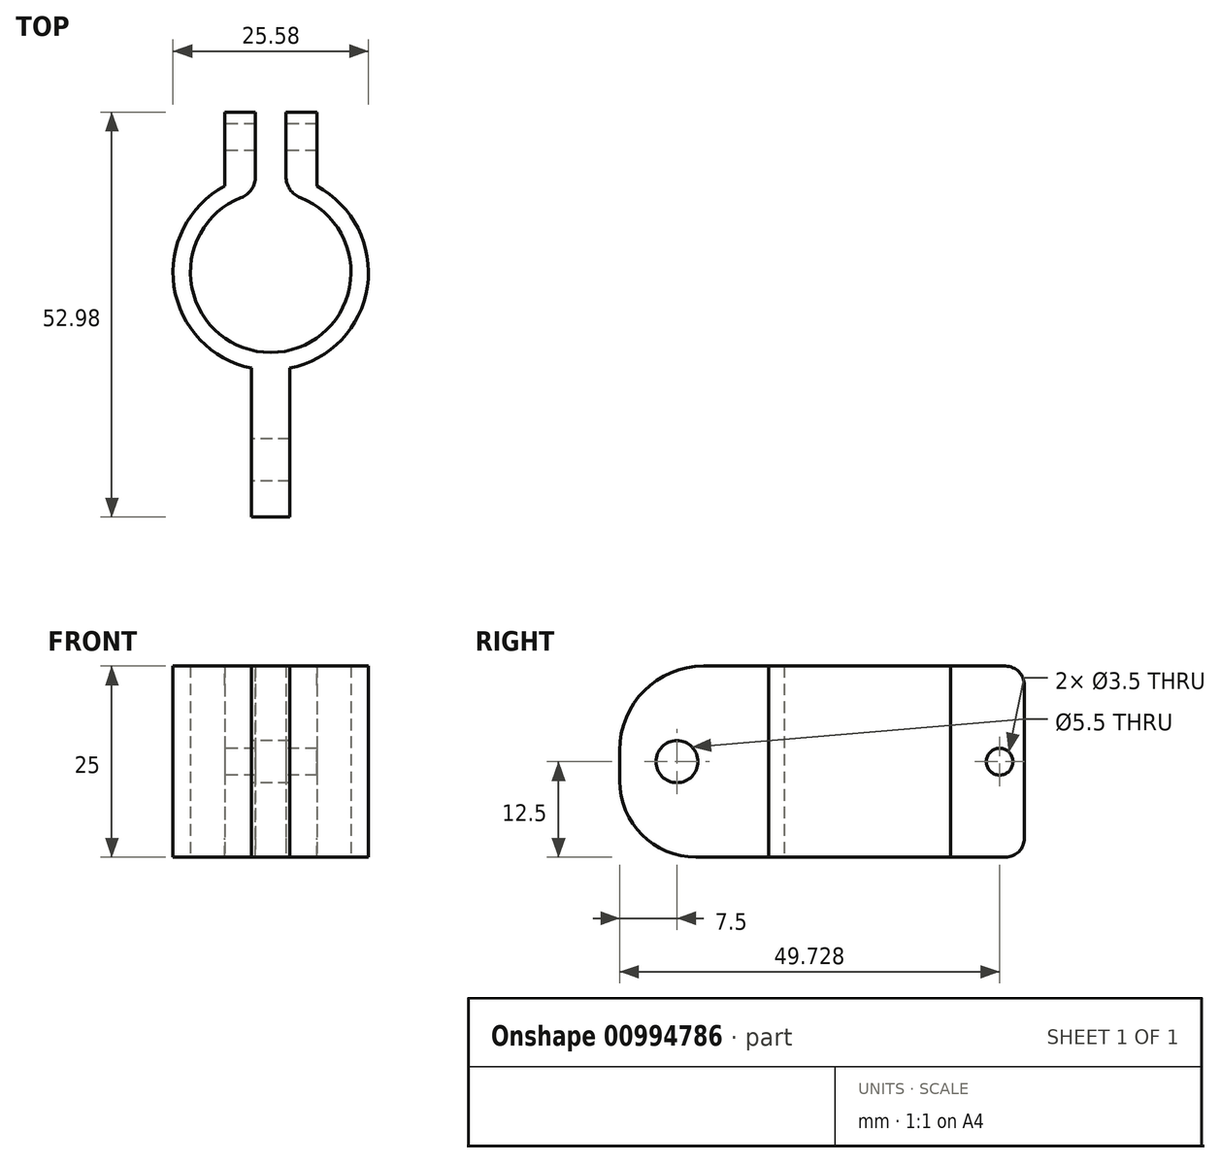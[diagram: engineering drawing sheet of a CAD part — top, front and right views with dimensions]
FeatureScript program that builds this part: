
annotation { "Feature Type Name" : "Feature", "Feature Type Description" : "" }
export const myFeature = defineFeature(function(context is Context, id is Id, definition is map)
    precondition{}
    {
        {
            var Q0;
            Q0=qCreatedBy(makeId("Top.planeOp"),FACE);
            var sketch = newSketch(context, id + "F0", { "sketchPlane" : qUnion([Q0])});
            skLineSegment(sketch, "E0", {"start": v(-2, 10.3) * mm, "end": v(-2, 20.94) * mm});
            skLineSegment(sketch, "E1.MirrorCS", {"start": v(2, 10.3) * mm, "end": v(2, 20.94) * mm});
            skArc(sketch, "E2", {"start": v(-2, 10.3) * mm, "mid": v(0, -10.5) * mm, "end": v(2, 10.3) * mm});
            skLineSegment(sketch, "E3", {"start": v(-2, 13.35) * mm, "end": v(-2, 13.35) * mm});
            skArc(sketch, "E4", {"start": v(-2, 12.63) * mm, "mid": v(0, -12.79) * mm, "end": v(2, 12.63) * mm});
            skLineSegment(sketch, "E5", {"start": v(-2, 10.3) * mm, "end": v(-2, 10.3) * mm});
            skLineSegment(sketch, "E6", {"start": v(-2, 12.63) * mm, "end": v(-2, 12.63) * mm});
            skLineSegment(sketch, "E7", {"start": v(2, 10.3) * mm, "end": v(2, 10.3) * mm});
            skLineSegment(sketch, "E8", {"start": v(2, 12.63) * mm, "end": v(2, 13.35) * mm});
            skLineSegment(sketch, "E9", {"start": v(-2.5, -12.54) * mm, "end": v(-2.5, -32.04) * mm});
            skLineSegment(sketch, "E10", {"start": v(-2.5, -32.04) * mm, "end": v(0, -32.04) * mm});
            skLineSegment(sketch, "E11.MirrorCS", {"start": v(2.5, -12.54) * mm, "end": v(2.5, -32.04) * mm});
            skLineSegment(sketch, "E12.MirrorCS", {"start": v(2.5, -32.04) * mm, "end": v(0, -32.04) * mm});
            skLineSegment(sketch, "E13.bottom", {"start": v(6.03, 20.94) * mm, "end": v(2, 20.94) * mm});
            skLineSegment(sketch, "E13.left", {"start": v(6.03, 20.94) * mm, "end": v(6.03, 8.6) * mm});
            skLineSegment(sketch, "E13.right", {"start": v(-6.03, 20.94) * mm, "end": v(-6.03, 8.6) * mm});
            skPoint(sketch, "E14.orphan", {"position": v(-2, 10.3) * mm});
            skPoint(sketch, "E15.orphan", {"position": v(2, 10.3) * mm});
            skLineSegment(sketch, "E16.trimOffspring", {"start": v(-2, 20.94) * mm, "end": v(-6.03, 20.94) * mm});
            skSolve(sketch);
        }
        {
            var Q0;
            {var subQ1=sQuery(id+"F0.wireOp",EDGE,"E9");Q0=makeQuery(id+"F0.imprint","IMPRINT",FACE,{"disambiguationData":[TD([[makeQuery(id+"F0.imprint","IMPRINT",EDGE,{"derivedFrom":subQ1}),1.0]])]});}
            var Q1;
            {var subQ0=sQuery(id+"F0.wireOp",EDGE,"E4");var subQ1=sQuery(id+"F0.wireOp",EDGE,"E0");var subQ2=makeQuery(id+"F0.imprint","INTERSECT",VERTEX,{"derivedFrom":[subQ1,subQ0]});var subQ9=sQuery(id+"F0.wireOp",EDGE,"E16.trimOffspring");Q1=qUnion([makeQuery(id+"F0.imprint","IMPRINT",FACE,{"disambiguationData":[TD([[makeQuery(id+"F0.imprint","IMPRINT",EDGE,{"derivedFrom":subQ9}),1.0]])]}),makeQuery(id+"F0.imprint","IMPRINT",FACE,{"disambiguationData":[TD([[makeQuery(id+"F0.imprint","IMPRINT",EDGE,{"disambiguationData":[TD([[subQ2,1.0]])],"derivedFrom":subQ1}),1.0]])]})]);}
            var Q2;
            {var subQ0=sQuery(id+"F0.wireOp",EDGE,"E2");var subQ1=sQuery(id+"F0.wireOp",EDGE,"E1.MirrorCS");var subQ2=makeQuery(id+"F0.imprint","INTERSECT",VERTEX,{"derivedFrom":[subQ1,subQ0]});Q2=makeQuery(id+"F0.imprint","IMPRINT",FACE,{"disambiguationData":[TD([[makeQuery(id+"F0.imprint","IMPRINT",EDGE,{"disambiguationData":[TD([[subQ2,-1.0]])],"derivedFrom":subQ1}),-1.0]])]});}
            var Q3;
            {var subQ6=sQuery(id+"F0.wireOp",EDGE,"E13.bottom");Q3=makeQuery(id+"F0.imprint","IMPRINT",FACE,{"disambiguationData":[TD([[makeQuery(id+"F0.imprint","IMPRINT",EDGE,{"derivedFrom":subQ6}),1.0]])]});}
            var Q4;
            {var subQ5=sQuery(id+"F0.wireOp",EDGE,"E2");var subQ7=sQuery(id+"F0.wireOp",EDGE,"E13.left");var subQ9=makeQuery(id+"F0.imprint","INTERSECT",VERTEX,{"derivedFrom":[subQ5,subQ7]});Q4=makeQuery(id+"F0.imprint","IMPRINT",FACE,{"disambiguationData":[TD([[makeQuery(id+"F0.imprint","IMPRINT",EDGE,{"disambiguationData":[TD([[subQ9,1.0]])],"derivedFrom":subQ5}),-1.0]])]});}
            extrude(context, id + "F1", {"entities" : qUnion([Q0, Q1, Q2, Q3, Q4]), "depth" : 25 * mm, "offsetDistance" : 25 * mm});
        }
        {
            var Q0;
            Q0=makeQuery(id+"F1.opExtrude","SWEPT_FACE",FACE,{"disambiguationData":[OSD([sQuery(id+"F0.wireOp",EDGE,"E13.right")])]});
            var sketch = newSketch(context, id + "F2", { "sketchPlane" : qUnion([Q0])});
            skCircle(sketch, "E17", {"center": v(24.54, 12.5) * mm, "radius": 2.75 * mm});
            skPoint(sketch, "E17.centerSnap0", {"position": v(32.04, 12.5) * mm});
            skLineSegment(sketch, "E18.0.0", {"start": v(-20.94, 0) * mm, "end": v(-11.28, 0) * mm});
            skLineSegment(sketch, "E18.0.1", {"start": v(-11.28, 0) * mm, "end": v(-11.28, 25) * mm});
            skLineSegment(sketch, "E18.0.2", {"start": v(-11.28, 25) * mm, "end": v(-20.94, 25) * mm});
            skLineSegment(sketch, "E18.0.3", {"start": v(-20.94, 25) * mm, "end": v(-20.94, 0) * mm});
            skCircle(sketch, "E19", {"center": v(-17.69, 12.5) * mm, "radius": 1.75 * mm});
            skPoint(sketch, "E19.centerSnap0", {"position": v(-20.94, 12.5) * mm});
            skPoint(sketch, "E19.centerSnap1", {"position": v(-16.1, 0) * mm});
            skSolve(sketch);
        }
        {
            var Q0;
            Q0=makeQuery(id+"F2.imprint","IMPRINT",FACE,{"disambiguationData":[TD([[makeQuery(id+"F2.imprint","IMPRINT",EDGE,{"derivedFrom":sQuery(id+"F2.wireOp",EDGE,"E17")}),1.0]])]});
            var Q1;
            Q1=makeQuery(id+"F2.imprint","IMPRINT",FACE,{"disambiguationData":[TD([[makeQuery(id+"F2.imprint","IMPRINT",EDGE,{"derivedFrom":sQuery(id+"F2.wireOp",EDGE,"E19")}),1.0]])]});
            extrude(context, id + "F3", {"entities" : qUnion([Q0, Q1]), "operationType" : NewBodyOperationType.REMOVE, "oppositeDirection" : true, "depth" : 50 * mm, "offsetDistance" : 25 * mm});
        }
        {
            var Q0;
            Q0=makeQuery(id+"F1.opExtrude","CAP_EDGE",EDGE,{"disambiguationData":[OSD([sQuery(id+"F0.wireOp",EDGE,"E10"),sQuery(id+"F0.wireOp",EDGE,"E12.MirrorCS")])],"isStart":false});
            fillet(context, id + "F4", {"entities" : qUnion([Q0]), "radius" : 11 * mm, "tangentPropagation" : true, "allowEdgeOverflow" : false});
        }
        {
            var Q0;
            Q0=makeQuery(id+"F1.opExtrude","CAP_EDGE",EDGE,{"disambiguationData":[OSD([sQuery(id+"F0.wireOp",EDGE,"E10"),sQuery(id+"F0.wireOp",EDGE,"E12.MirrorCS")])],"isStart":true});
            fillet(context, id + "F5", {"entities" : qUnion([Q0]), "radius" : 10 * mm, "tangentPropagation" : true, "allowEdgeOverflow" : false});
        }
        {
            var Q0;
            Q0=makeQuery(id+"F1.opExtrude","CAP_EDGE",EDGE,{"disambiguationData":[OSD([sQuery(id+"F0.wireOp",EDGE,"E16.trimOffspring")])],"isStart":false});
            var Q1;
            Q1=makeQuery(id+"F1.opExtrude","CAP_EDGE",EDGE,{"disambiguationData":[OSD([sQuery(id+"F0.wireOp",EDGE,"E13.bottom")])],"isStart":false});
            var Q2;
            Q2=makeQuery(id+"F1.opExtrude","CAP_EDGE",EDGE,{"disambiguationData":[OSD([sQuery(id+"F0.wireOp",EDGE,"E13.bottom")])],"isStart":true});
            var Q3;
            Q3=makeQuery(id+"F1.opExtrude","CAP_EDGE",EDGE,{"disambiguationData":[OSD([sQuery(id+"F0.wireOp",EDGE,"E16.trimOffspring")])],"isStart":true});
            fillet(context, id + "F6", {"entities" : qUnion([Q0, Q1, Q2, Q3]), "radius" : 2.5 * mm, "tangentPropagation" : true, "allowEdgeOverflow" : false});
        }
        {
            var Q0;
            Q0=makeQuery(id+"F1.opExtrude","SWEPT_EDGE",EDGE,{"disambiguationData":[OSD([sQuery(id+"F0.wireOp",EDGE,"E0"),sQuery(id+"F0.wireOp",EDGE,"E2")])]});
            var Q1;
            Q1=makeQuery(id+"F1.opExtrude","SWEPT_EDGE",EDGE,{"disambiguationData":[OSD([sQuery(id+"F0.wireOp",EDGE,"E1.MirrorCS"),sQuery(id+"F0.wireOp",EDGE,"E2")])]});
            fillet(context, id + "F7", {"entities" : qUnion([Q0, Q1]), "radius" : 3 * mm, "tangentPropagation" : true, "allowEdgeOverflow" : false});
        }
    });
